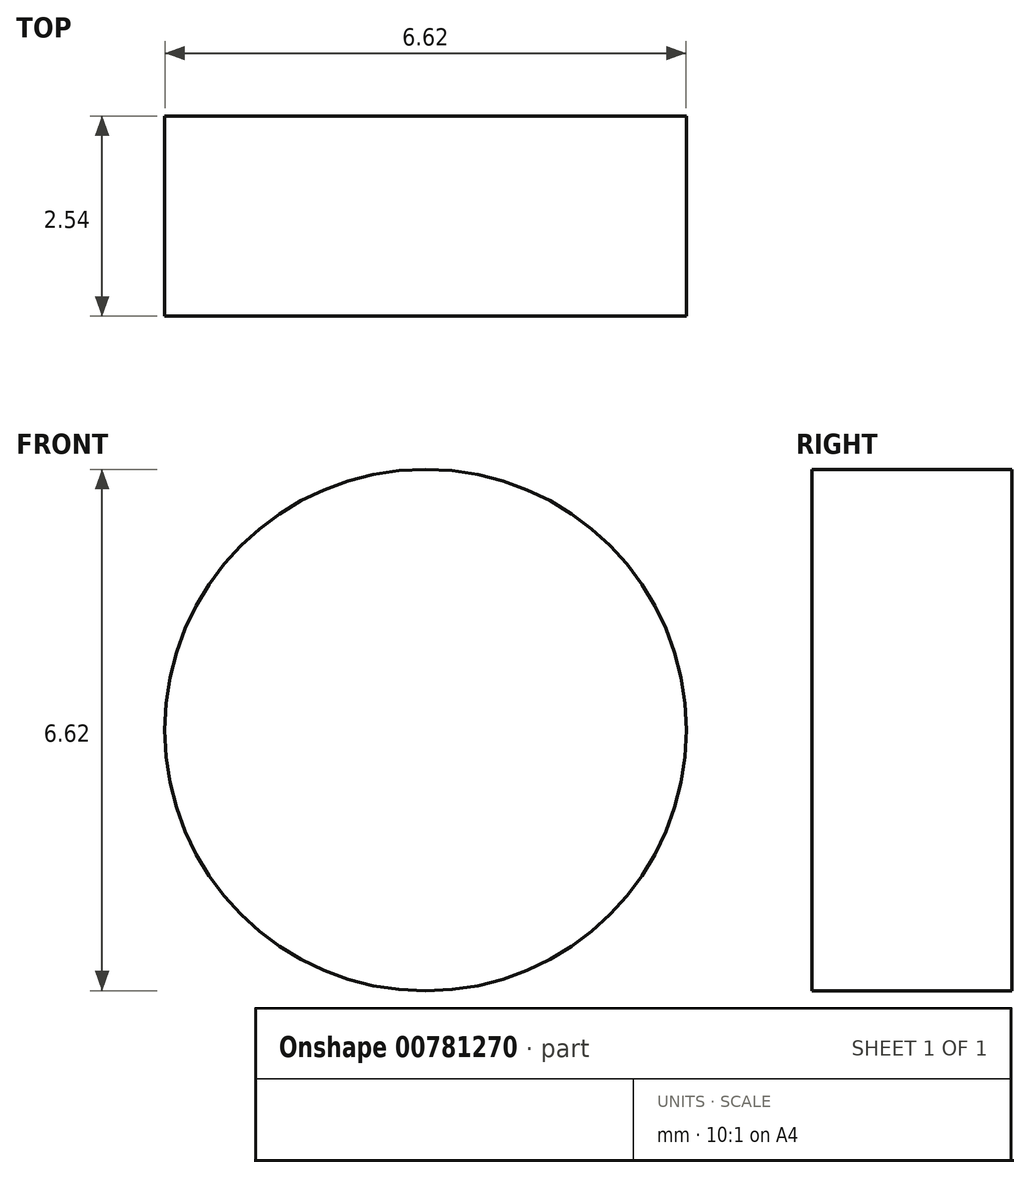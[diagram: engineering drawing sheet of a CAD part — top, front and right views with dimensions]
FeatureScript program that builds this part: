
annotation { "Feature Type Name" : "Feature", "Feature Type Description" : "" }
export const myFeature = defineFeature(function(context is Context, id is Id, definition is map)
    precondition{}
    {
        {
            var Q0;
            Q0=qCreatedBy(makeId("Front.planeOp"),FACE);
            var sketch = newSketch(context, id + "F0", { "sketchPlane" : qUnion([Q0])});
            skCircle(sketch, "E0", {"center": v(0, 0) * mm, "radius": 3.31 * mm});
            skSolve(sketch);
        }
        {
            var Q0;
            Q0=qCreatedBy(makeId("Top.planeOp"),FACE);
            var sketch = newSketch(context, id + "F1", { "sketchPlane" : qUnion([Q0])});
            skFitSpline(sketch, "E1", {"points": [v(0, 0) * mm, v(3.3, 5.34) * mm, v(11.7, 7.16) * mm, v(19.66, 7.61) * mm, v(26.03, 7.84) * mm], "startDerivative": vector(10.05, 26.73) * mm, "endDerivative": vector(26.73, 0.81) * mm});
            skFitSpline(sketch, "E2", {"points": [v(0, 0) * mm, v(2.61, -6.48) * mm, v(11.7, -9.89) * mm, v(19.66, -11.48) * mm, v(28.98, -12.16) * mm, v(37.4, -13.3) * mm, v(45.35, -17.16) * mm, v(48.3, -20.34) * mm], "startDerivative": vector(9.74, -54.12) * mm, "endDerivative": vector(22.48, -29.98) * mm});
            skSolve(sketch);
        }
        {
            var Q0;
            Q0 = qConstructionFilter(qBodyType(qCreatedBy(id + "F0" ,EDGE), BodyType.WIRE), ConstructionObject.NO);
            extrude(context, id + "F2", {"bodyType" : ToolBodyType.SURFACE, "surfaceEntities" : qUnion([Q0]), "endBound" : BoundingType.SYMMETRIC, "depth" : 2.54 * mm, "offsetDistance" : 25.4 * mm});
        }
    });
